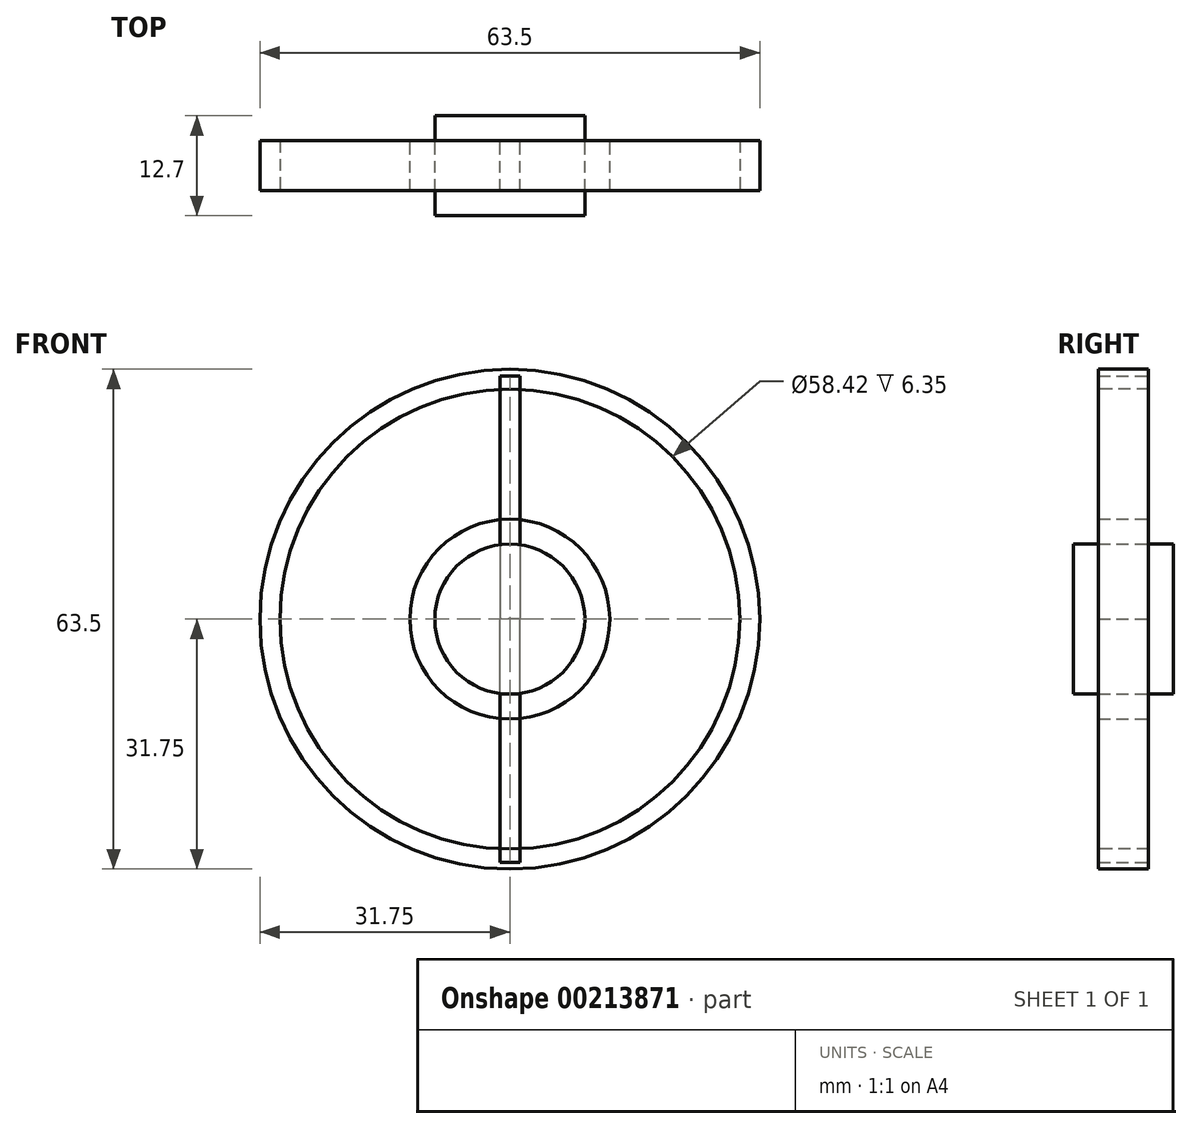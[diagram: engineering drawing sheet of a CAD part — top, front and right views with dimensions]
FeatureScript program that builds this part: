
annotation { "Feature Type Name" : "Feature", "Feature Type Description" : "" }
export const myFeature = defineFeature(function(context is Context, id is Id, definition is map)
    precondition{}
    {
        {
            var Q0;
            Q0=qCreatedBy(makeId("Front.planeOp"),FACE);
            var sketch = newSketch(context, id + "F0", { "sketchPlane" : qUnion([Q0])});
            skCircle(sketch, "E0", {"center": v(0, 0) * mm, "radius": 31.75 * mm});
            skSolve(sketch);
        }
        {
            var Q0;
            Q0=makeQuery(id+"F0.imprint","IMPRINT",FACE,{"disambiguationData":[TD([[makeQuery(id+"F0.imprint","IMPRINT",EDGE,{"derivedFrom":sQuery(id+"F0.wireOp",EDGE,"E0")}),1.0]])]});
            extrude(context, id + "F1", {"entities" : qUnion([Q0]), "endBound" : BoundingType.SYMMETRIC, "depth" : 6.35 * mm});
        }
        {
            var Q0;
            Q0=makeQuery(id+"F1.opExtrude","CAP_FACE",FACE,{"disambiguationData":[OSD([sQuery(id+"F0.wireOp",EDGE,"E0")])],"isStart":false});
            var sketch = newSketch(context, id + "F2", { "sketchPlane" : qUnion([Q0])});
            skCircle(sketch, "E1", {"center": v(0, 0) * mm, "radius": 29.21 * mm});
            skSolve(sketch);
        }
        {
            var Q0;
            Q0=makeQuery(id+"F2.imprint","IMPRINT",FACE,{"disambiguationData":[TD([[makeQuery(id+"F2.imprint","IMPRINT",EDGE,{"derivedFrom":sQuery(id+"F2.wireOp",EDGE,"E1")}),1.0]])]});
            extrude(context, id + "F3", {"entities" : qUnion([Q0]), "operationType" : NewBodyOperationType.REMOVE, "endBound" : BoundingType.THROUGH_ALL, "oppositeDirection" : true, "depth" : 25.4 * mm});
        }
        {
            var Q0;
            Q0=qCreatedBy(makeId("Front.planeOp"),FACE);
            var sketch = newSketch(context, id + "F4", { "sketchPlane" : qUnion([Q0])});
            skCircle(sketch, "E2", {"center": v(0, 0) * mm, "radius": 12.7 * mm});
            skSolve(sketch);
        }
        {
            var Q0;
            Q0=makeQuery(id+"F4.imprint","IMPRINT",FACE,{"disambiguationData":[TD([[makeQuery(id+"F4.imprint","IMPRINT",EDGE,{"derivedFrom":sQuery(id+"F4.wireOp",EDGE,"E2")}),1.0]])]});
            extrude(context, id + "F5", {"entities" : qUnion([Q0]), "endBound" : BoundingType.SYMMETRIC, "depth" : 6.35 * mm});
        }
        {
            var Q0;
            Q0=qCreatedBy(makeId("Front.planeOp"),FACE);
            var sketch = newSketch(context, id + "F6", { "sketchPlane" : qUnion([Q0])});
            skLineSegment(sketch, "E3", {"start": v(0, 30.92) * mm, "end": v(-1.27, 30.92) * mm});
            skLineSegment(sketch, "E4", {"start": v(-1.27, 30.92) * mm, "end": v(-1.27, 0) * mm});
            skLineSegment(sketch, "E5", {"start": v(-1.27, 0) * mm, "end": v(0, 0) * mm});
            skLineSegment(sketch, "E6.MirrorCS", {"start": v(1.27, 30.92) * mm, "end": v(1.27, 0) * mm});
            skLineSegment(sketch, "E7", {"start": v(1.27, 30.92) * mm, "end": v(0, 30.92) * mm});
            skLineSegment(sketch, "E8", {"start": v(1.27, 0) * mm, "end": v(0, 0) * mm});
            skSolve(sketch);
        }
        {
            var Q0;
            Q0=makeQuery(id+"F6.imprint","IMPRINT",FACE,{"disambiguationData":[TD([[makeQuery(id+"F6.imprint","IMPRINT",EDGE,{"derivedFrom":sQuery(id+"F6.wireOp",EDGE,"E3")}),1.0]])]});
            extrude(context, id + "F7", {"entities" : qUnion([Q0]), "endBound" : BoundingType.SYMMETRIC, "depth" : 6.35 * mm});
        }
        {
            var Q0;
            Q0=makeQuery(id+"F7.opExtrude","SWEPT_BODY",BODY,{"disambiguationData":[OSD([sQuery(id+"F6.wireOp",EDGE,"E3"),sQuery(id+"F6.wireOp",EDGE,"E4"),sQuery(id+"F6.wireOp",EDGE,"E5"),sQuery(id+"F6.wireOp",EDGE,"E6.MirrorCS"),sQuery(id+"F6.wireOp",EDGE,"E7"),sQuery(id+"F6.wireOp",EDGE,"E8")])]});
            var Q1;
            Q1=makeQuery(id+"F5.opExtrude","CAP_EDGE",EDGE,{"disambiguationData":[OSD([sQuery(id+"F4.wireOp",EDGE,"E2")])],"isStart":false});
            circularPattern(context, id + "F8", {"entities" : qUnion([Q0]), "axis" : qUnion([Q1]), "angle" : 360 * degree, "instanceCount" : 2, "equalSpace" : true});
        }
        {
            var Q0;
            Q0=qCreatedBy(makeId("Front.planeOp"),FACE);
            var sketch = newSketch(context, id + "F9", { "sketchPlane" : qUnion([Q0])});
            skCircle(sketch, "E9", {"center": v(0, 0) * mm, "radius": 9.53 * mm});
            skSolve(sketch);
        }
        {
            var Q0;
            Q0 = qSketchRegion(id + "F9", true);
            extrude(context, id + "F10", {"entities" : qUnion([Q0]), "endBound" : BoundingType.SYMMETRIC, "depth" : 12.7 * mm});
        }
    });
